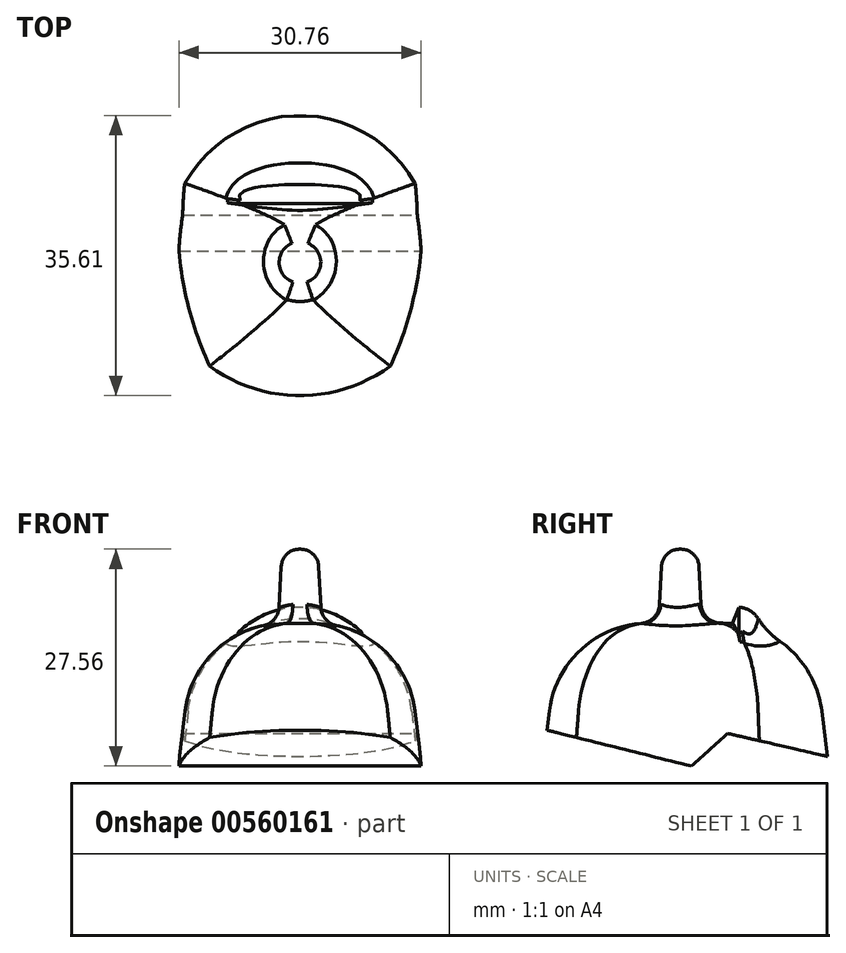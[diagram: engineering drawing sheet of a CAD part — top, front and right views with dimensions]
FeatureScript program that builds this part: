
annotation { "Feature Type Name" : "Feature", "Feature Type Description" : "" }
export const myFeature = defineFeature(function(context is Context, id is Id, definition is map)
    precondition{}
    {
        {
            var Q0;
            Q0=qCreatedBy(makeId("Top.planeOp"),FACE);
            var sketch = newSketch(context, id + "F0", { "sketchPlane" : qUnion([Q0])});
            skLineSegment(sketch, "E0", {"start": v(0, 17.2) * mm, "end": v(0, -20.9) * mm, "construction": true});
            skLineSegment(sketch, "E1", {"start": v(0, -20.9) * mm, "end": v(11.1, -20.9) * mm, "construction": true});
            skLineSegment(sketch, "E2", {"start": v(0, 17.2) * mm, "end": v(9.05, 17.2) * mm, "construction": true});
            skArc(sketch, "E3", {"start": v(0, 17.2) * mm, "mid": v(-9.19, 14.72) * mm, "end": v(-15.88, 7.95) * mm});
            skArc(sketch, "E4", {"start": v(-12.56, -16.55) * mm, "mid": v(-6.64, -19.78) * mm, "end": v(0, -20.9) * mm});
            skArc(sketch, "E5", {"start": v(-15.88, 7.95) * mm, "mid": v(-15.94, -4.54) * mm, "end": v(-12.56, -16.55) * mm});
            skLineSegment(sketch, "E6.MirrorCS", {"start": v(0, -20.9) * mm, "end": v(-11.1, -20.9) * mm, "construction": true});
            skLineSegment(sketch, "E7.MirrorCS", {"start": v(0, 17.2) * mm, "end": v(-9.05, 17.2) * mm, "construction": true});
            skArc(sketch, "E8.MirrorCS", {"start": v(15.88, 7.95) * mm, "mid": v(15.94, -4.54) * mm, "end": v(12.56, -16.55) * mm});
            skArc(sketch, "E9.MirrorCS", {"start": v(0, 17.2) * mm, "mid": v(9.19, 14.72) * mm, "end": v(15.88, 7.95) * mm});
            skArc(sketch, "E10.MirrorCS", {"start": v(12.56, -16.55) * mm, "mid": v(6.64, -19.78) * mm, "end": v(0, -20.9) * mm});
            skSolve(sketch);
        }
        {
            var Q0;
            Q0=makeQuery(id+"F0.imprint","IMPRINT",FACE,{"disambiguationData":[TD([[makeQuery(id+"F0.imprint","IMPRINT",EDGE,{"derivedFrom":sQuery(id+"F0.wireOp",EDGE,"E3")}),1.0]])]});
            extrude(context, id + "F1", {"entities" : qUnion([Q0]), "depth" : 25.4 * mm, "offsetDistance" : 25.4 * mm, "hasDraft" : true, "draftAngle" : 7 * degree, "draftPullDirection" : true});
        }
        {
            var Q0;
            Q0=makeQuery(id+"F1.opExtrude","CAP_FACE",FACE,{"disambiguationData":[OSD([sQuery(id+"F0.wireOp",EDGE,"E3"),sQuery(id+"F0.wireOp",EDGE,"E4"),sQuery(id+"F0.wireOp",EDGE,"E5"),sQuery(id+"F0.wireOp",EDGE,"E8.MirrorCS"),sQuery(id+"F0.wireOp",EDGE,"E9.MirrorCS"),sQuery(id+"F0.wireOp",EDGE,"E10.MirrorCS")])],"isStart":false});
            fillet(context, id + "F2", {"entities" : qUnion([Q0]), "radius" : 12.7 * mm, "tangentPropagation" : true, "allowEdgeOverflow" : false});
        }
        {
            var Q0;
            Q0=makeQuery(id+"F1.opExtrude","CAP_FACE",FACE,{"disambiguationData":[OSD([sQuery(id+"F0.wireOp",EDGE,"E3"),sQuery(id+"F0.wireOp",EDGE,"E4"),sQuery(id+"F0.wireOp",EDGE,"E5"),sQuery(id+"F0.wireOp",EDGE,"E8.MirrorCS"),sQuery(id+"F0.wireOp",EDGE,"E9.MirrorCS"),sQuery(id+"F0.wireOp",EDGE,"E10.MirrorCS")])],"isStart":false});
            var sketch = newSketch(context, id + "F3", { "sketchPlane" : qUnion([Q0])});
            skCircle(sketch, "E11", {"center": v(0, -2.52) * mm, "radius": 2.76 * mm});
            skPoint(sketch, "E11.centerSnap0", {"position": v(0, -6.54) * mm});
            skSolve(sketch);
        }
        {
            var Q0;
            Q0 = qSketchRegion(id + "F3", true);
            extrude(context, id + "F4", {"entities" : qUnion([Q0]), "operationType" : NewBodyOperationType.ADD, "depth" : 9.4 * mm, "offsetDistance" : 25.4 * mm, "hasDraft" : true, "draftAngle" : 3 * degree, "draftPullDirection" : true, "hasSecondDirection" : true, "secondDirectionOppositeDirection" : true, "secondDirectionDepth" : 12.7 * mm, "hasSecondDirectionDraft" : true, "secondDirectionDraftAngle" : 3 * degree});
        }
        {
            var Q0;
            {var subQ0=makeQuery(id+"F4.opExtrude","SWEPT_FACE",FACE,{"disambiguationData":[OSD([sQuery(id+"F3.wireOp",EDGE,"E11")])]});Q0=makeQuery(id+"F4.boolean.opBoolean","INTERSECT",EDGE,{"disambiguationData":[OD(1.0)],"derivedFrom":[makeQuery(id+"F1.opExtrude","CAP_FACE",FACE,{"disambiguationData":[OSD([sQuery(id+"F0.wireOp",EDGE,"E3"),sQuery(id+"F0.wireOp",EDGE,"E4"),sQuery(id+"F0.wireOp",EDGE,"E5"),sQuery(id+"F0.wireOp",EDGE,"E8.MirrorCS"),sQuery(id+"F0.wireOp",EDGE,"E9.MirrorCS"),sQuery(id+"F0.wireOp",EDGE,"E10.MirrorCS")])],"isStart":false}),makeQuery(id+"F4.*.booleanUnion.opBoolean","MERGE",FACE,{"derivedFrom":[makeQuery(id+"F4.*.split.splitOp","SPLIT",FACE,{"derivedFrom":subQ0}),makeQuery(id+"F4.*.split.splitOp","SPLIT",FACE,{"derivedFrom":subQ0,"isFromBackBody":true})]})]});}
            var Q1;
            {var subQ0=makeQuery(id+"F4.opExtrude","SWEPT_FACE",FACE,{"disambiguationData":[OSD([sQuery(id+"F3.wireOp",EDGE,"E11")])]});Q1=makeQuery(id+"F4.boolean.opBoolean","INTERSECT",EDGE,{"derivedFrom":[makeQuery(id+"F2.opFillet","BLEND_FACE",FACE,{"disambiguationData":[OSD([sQuery(id+"F0.wireOp",EDGE,"E5")])]}),makeQuery(id+"F4.*.booleanUnion.opBoolean","MERGE",FACE,{"derivedFrom":[makeQuery(id+"F4.*.split.splitOp","SPLIT",FACE,{"derivedFrom":subQ0}),makeQuery(id+"F4.*.split.splitOp","SPLIT",FACE,{"derivedFrom":subQ0,"isFromBackBody":true})]})]});}
            var Q2;
            {var subQ0=makeQuery(id+"F4.opExtrude","SWEPT_FACE",FACE,{"disambiguationData":[OSD([sQuery(id+"F3.wireOp",EDGE,"E11")])]});Q2=makeQuery(id+"F4.boolean.opBoolean","INTERSECT",EDGE,{"disambiguationData":[OD(0.0)],"derivedFrom":[makeQuery(id+"F1.opExtrude","CAP_FACE",FACE,{"disambiguationData":[OSD([sQuery(id+"F0.wireOp",EDGE,"E3"),sQuery(id+"F0.wireOp",EDGE,"E4"),sQuery(id+"F0.wireOp",EDGE,"E5"),sQuery(id+"F0.wireOp",EDGE,"E8.MirrorCS"),sQuery(id+"F0.wireOp",EDGE,"E9.MirrorCS"),sQuery(id+"F0.wireOp",EDGE,"E10.MirrorCS")])],"isStart":false}),makeQuery(id+"F4.*.booleanUnion.opBoolean","MERGE",FACE,{"derivedFrom":[makeQuery(id+"F4.*.split.splitOp","SPLIT",FACE,{"derivedFrom":subQ0}),makeQuery(id+"F4.*.split.splitOp","SPLIT",FACE,{"derivedFrom":subQ0,"isFromBackBody":true})]})]});}
            var Q3;
            {var subQ0=makeQuery(id+"F4.opExtrude","SWEPT_FACE",FACE,{"disambiguationData":[OSD([sQuery(id+"F3.wireOp",EDGE,"E11")])]});Q3=makeQuery(id+"F4.boolean.opBoolean","INTERSECT",EDGE,{"derivedFrom":[makeQuery(id+"F2.opFillet","BLEND_FACE",FACE,{"disambiguationData":[OSD([sQuery(id+"F0.wireOp",EDGE,"E8.MirrorCS")])]}),makeQuery(id+"F4.*.booleanUnion.opBoolean","MERGE",FACE,{"derivedFrom":[makeQuery(id+"F4.*.split.splitOp","SPLIT",FACE,{"derivedFrom":subQ0}),makeQuery(id+"F4.*.split.splitOp","SPLIT",FACE,{"derivedFrom":subQ0,"isFromBackBody":true})]})]});}
            fillet(context, id + "F5", {"entities" : qUnion([Q0, Q1, Q2, Q3]), "radius" : 2.54 * mm, "tangentPropagation" : true, "allowEdgeOverflow" : false});
        }
        {
            var Q0;
            Q0=makeQuery(id+"F4.opExtrude","CAP_FACE",FACE,{"disambiguationData":[OSD([sQuery(id+"F3.wireOp",EDGE,"E11")])],"isStart":false});
            fillet(context, id + "F6", {"entities" : qUnion([Q0]), "radius" : 2.3 * mm, "tangentPropagation" : true, "allowEdgeOverflow" : false});
        }
        {
            var Q0;
            Q0=qCreatedBy(makeId("Right.planeOp"),FACE);
            var sketch = newSketch(context, id + "F7", { "sketchPlane" : qUnion([Q0])});
            skArc(sketch, "E12", {"start": v(7.79, 23.56) * mm, "mid": v(7.27, 26.15) * mm, "end": v(4.96, 27.42) * mm});
            skLineSegment(sketch, "E13", {"start": v(4.96, 27.42) * mm, "end": v(2.97, 22.6) * mm});
            skLineSegment(sketch, "E14", {"start": v(2.97, 22.6) * mm, "end": v(7.79, 23.56) * mm});
            skLineSegment(sketch, "E15", {"start": v(2.45, 16.22) * mm, "end": v(8.19, 16.22) * mm});
            skSolve(sketch);
        }
        {
            var Q0;
            Q0=makeQuery(id+"F7.imprint","IMPRINT",FACE,{"disambiguationData":[TD([[makeQuery(id+"F7.imprint","IMPRINT",EDGE,{"derivedFrom":sQuery(id+"F7.wireOp",EDGE,"E12")}),1.0]])]});
            var Q1;
            Q1=sQuery(id+"F7.wireOp",EDGE,"E15");
            revolve(context, id + "F8", {"operationType" : NewBodyOperationType.ADD, "entities" : qUnion([Q0]), "axis" : qUnion([Q1]), "revolveType" : RevolveType.FULL});
        }
        {
            var Q0;
            Q0=makeQuery(id+"F8.boolean.opBoolean","INTERSECT",EDGE,{"derivedFrom":[makeQuery(id+"F2.opFillet","BLEND_FACE",FACE,{"disambiguationData":[OSD([sQuery(id+"F0.wireOp",EDGE,"E3"),sQuery(id+"F0.wireOp",EDGE,"E9.MirrorCS")])]}),makeQuery(id+"F8.opRevolve","SWEPT_FACE",FACE,{"disambiguationData":[OSD([sQuery(id+"F7.wireOp",EDGE,"E12")])]})]});
            var Q1;
            Q1=makeQuery(id+"F8.boolean.opBoolean","INTERSECT",EDGE,{"derivedFrom":[makeQuery(id+"F2.opFillet","BLEND_FACE",FACE,{"disambiguationData":[OSD([sQuery(id+"F0.wireOp",EDGE,"E8.MirrorCS")])]}),makeQuery(id+"F8.opRevolve","SWEPT_FACE",FACE,{"disambiguationData":[OSD([sQuery(id+"F7.wireOp",EDGE,"E12")])]})]});
            var Q2;
            Q2=makeQuery(id+"F8.boolean.opBoolean","INTERSECT",EDGE,{"derivedFrom":[makeQuery(id+"F2.opFillet","BLEND_FACE",FACE,{"disambiguationData":[OSD([sQuery(id+"F0.wireOp",EDGE,"E5")])]}),makeQuery(id+"F8.opRevolve","SWEPT_FACE",FACE,{"disambiguationData":[OSD([sQuery(id+"F7.wireOp",EDGE,"E12")])]})]});
            fillet(context, id + "F9", {"entities" : qUnion([Q0, Q1, Q2]), "radius" : 10.16 * mm, "tangentPropagation" : true, "allowEdgeOverflow" : false});
        }
        {
            var Q0;
            Q0=qCreatedBy(makeId("Right.planeOp"),FACE);
            var sketch = newSketch(context, id + "F10", { "sketchPlane" : qUnion([Q0])});
            skLineSegment(sketch, "E16", {"start": v(-22.68, 12.61) * mm, "end": v(-1.1, 7.24) * mm});
            skLineSegment(sketch, "E17", {"start": v(-1.1, 7.24) * mm, "end": v(3.5, 11.4) * mm});
            skLineSegment(sketch, "E18", {"start": v(3.5, 11.4) * mm, "end": v(21.55, 7.24) * mm});
            skLineSegment(sketch, "E19", {"start": v(21.55, 7.24) * mm, "end": v(26.48, -11.25) * mm});
            skLineSegment(sketch, "E20", {"start": v(26.48, -11.25) * mm, "end": v(-32.75, -11.25) * mm});
            skLineSegment(sketch, "E21", {"start": v(-32.75, -11.25) * mm, "end": v(-22.68, 12.61) * mm});
            skSolve(sketch);
        }
        {
            var Q0;
            Q0=makeQuery(id+"F10.imprint","IMPRINT",FACE,{"disambiguationData":[TD([[makeQuery(id+"F10.imprint","IMPRINT",EDGE,{"derivedFrom":sQuery(id+"F10.wireOp",EDGE,"E16")}),-1.0]])]});
            extrude(context, id + "F11", {"entities" : qUnion([Q0]), "operationType" : NewBodyOperationType.REMOVE, "endBound" : BoundingType.SYMMETRIC, "oppositeDirection" : true, "depth" : 72.44 * mm, "offsetDistance" : 25.4 * mm});
        }
    });
